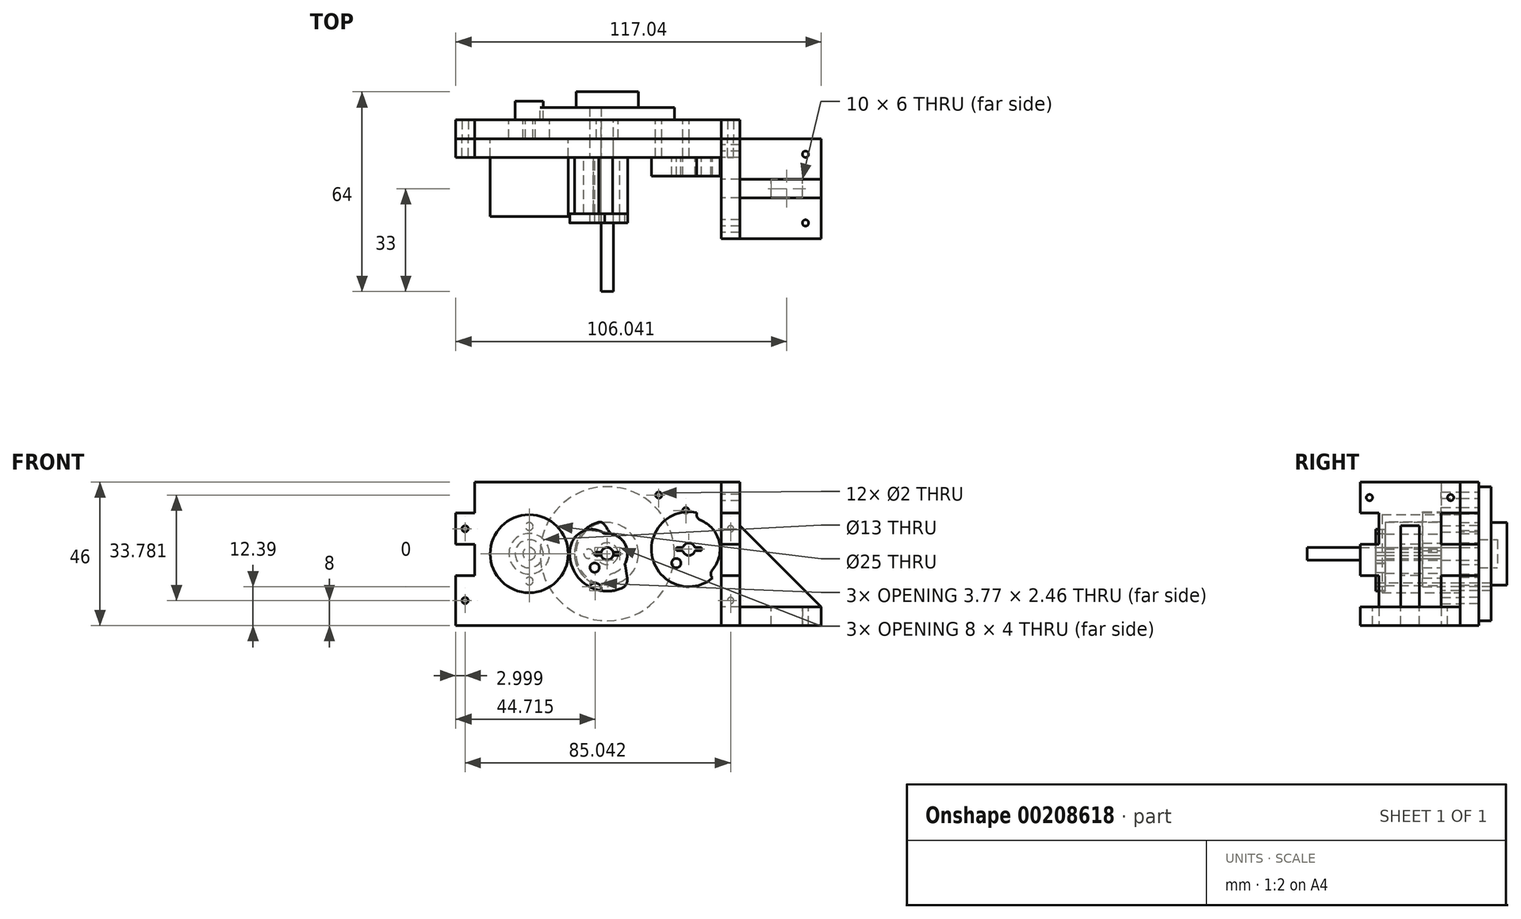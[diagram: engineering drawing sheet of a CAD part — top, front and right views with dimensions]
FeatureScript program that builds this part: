
annotation { "Feature Type Name" : "Feature", "Feature Type Description" : "" }
export const myFeature = defineFeature(function(context is Context, id is Id, definition is map)
    precondition{}
    {
        {
            var Q0;
            Q0=qCreatedBy(makeId("Front.planeOp"),FACE);
            var sketch = newSketch(context, id + "F0", { "sketchPlane" : qUnion([Q0])});
            skLineSegment(sketch, "E0.bottom", {"start": v(36.52, 23) * mm, "end": v(-42.52, 23) * mm});
            skLineSegment(sketch, "E0.top", {"start": v(42.52, -23) * mm, "end": v(-48.52, -23) * mm});
            skPoint(sketch, "E0.middle", {"position": v(0, 0) * mm});
            skCircle(sketch, "E1", {"center": v(-25, 0) * mm, "radius": 6.5 * mm});
            skLineSegment(sketch, "E2", {"start": v(-25, 8.75) * mm, "end": v(-25, -8.75) * mm, "construction": true});
            skCircle(sketch, "E3", {"center": v(-25, 8.75) * mm, "radius": 1.25 * mm});
            skCircle(sketch, "E4", {"center": v(-25, -8.75) * mm, "radius": 1.25 * mm});
            skCircle(sketch, "E5", {"center": v(0, 0) * mm, "radius": 3.5 * mm});
            skCircle(sketch, "E6", {"center": v(-25, 0) * mm, "radius": 12.5 * mm, "construction": true});
            skCircle(sketch, "E7", {"center": v(16.5, 18.78) * mm, "radius": 1 * mm});
            skCircle(sketch, "E8", {"center": v(25.19, 13.81) * mm, "radius": 1 * mm});
            skLineSegment(sketch, "E9", {"start": v(25.19, 13.81) * mm, "end": v(16.5, 18.78) * mm, "construction": true});
            skLineSegment(sketch, "E10.bottom", {"start": v(8.2, 14.32) * mm, "end": v(13.16, 23) * mm, "construction": true});
            skLineSegment(sketch, "E10.top", {"start": v(25.55, 4.39) * mm, "end": v(30.52, 13.07) * mm, "construction": true});
            skLineSegment(sketch, "E10.left", {"start": v(8.2, 14.32) * mm, "end": v(25.55, 4.39) * mm, "construction": true});
            skLineSegment(sketch, "E10.right", {"start": v(13.16, 23) * mm, "end": v(30.52, 13.07) * mm, "construction": true});
            skLineSegment(sketch, "E11", {"start": v(21.84, 18.03) * mm, "end": v(20.85, 16.3) * mm, "construction": true});
            skCircle(sketch, "E12", {"center": v(0, 0) * mm, "radius": 6.5 * mm, "construction": true});
            skCircle(sketch, "E13", {"center": v(0, 0) * mm, "radius": 10.5 * mm, "construction": true});
            skLineSegment(sketch, "E14", {"start": v(36.52, 23) * mm, "end": v(36.52, 13) * mm});
            skLineSegment(sketch, "E15", {"start": v(36.52, 13) * mm, "end": v(42.52, 13) * mm});
            skLineSegment(sketch, "E16", {"start": v(42.52, 13) * mm, "end": v(42.52, 3) * mm});
            skLineSegment(sketch, "E17", {"start": v(42.52, 3) * mm, "end": v(36.52, 3) * mm});
            skLineSegment(sketch, "E18", {"start": v(36.52, 3) * mm, "end": v(36.52, -7) * mm});
            skLineSegment(sketch, "E19", {"start": v(36.52, -7) * mm, "end": v(42.52, -7) * mm});
            skLineSegment(sketch, "E20", {"start": v(42.52, -7) * mm, "end": v(42.52, -23) * mm});
            skCircle(sketch, "E21", {"center": v(0, 0) * mm, "radius": 21.5 * mm, "construction": true});
            skLineSegment(sketch, "E22", {"start": v(-3, -23) * mm, "end": v(-3, -27.3) * mm, "construction": true});
            skLineSegment(sketch, "E23.MirrorCS", {"start": v(-42.52, 23) * mm, "end": v(-42.52, 13) * mm});
            skLineSegment(sketch, "E24.MirrorCS", {"start": v(-42.52, 13) * mm, "end": v(-48.52, 13) * mm});
            skLineSegment(sketch, "E25.MirrorCS", {"start": v(-48.52, 13) * mm, "end": v(-48.52, 3) * mm});
            skLineSegment(sketch, "E26.MirrorCS", {"start": v(-48.52, 3) * mm, "end": v(-42.52, 3) * mm});
            skLineSegment(sketch, "E27.MirrorCS", {"start": v(-42.52, 3) * mm, "end": v(-42.52, -7) * mm});
            skLineSegment(sketch, "E28.MirrorCS", {"start": v(-42.52, -7) * mm, "end": v(-48.52, -7) * mm});
            skLineSegment(sketch, "E29.MirrorCS", {"start": v(-48.52, -7) * mm, "end": v(-48.52, -23) * mm});
            skSolve(sketch);
        }
        {
            var Q0;
            Q0 = qSketchRegion(id + "F0", true);
            extrude(context, id + "F1", {"entities" : qUnion([Q0]), "depth" : 6 * mm});
        }
        {
            var Q0;
            Q0=qCreatedBy(makeId("Top.planeOp"),FACE);
            var sketch = newSketch(context, id + "F2", { "sketchPlane" : qUnion([Q0])});
            skLineSegment(sketch, "E30", {"start": v(0, 9) * mm, "end": v(0, -55) * mm});
            skLineSegment(sketch, "E31", {"start": v(0, -55) * mm, "end": v(2, -55) * mm});
            skLineSegment(sketch, "E32", {"start": v(2, -55) * mm, "end": v(2, 0) * mm});
            skLineSegment(sketch, "E33", {"start": v(2, 0) * mm, "end": v(21.5, 0) * mm});
            skLineSegment(sketch, "E34", {"start": v(21.5, 0) * mm, "end": v(21.5, 4) * mm});
            skLineSegment(sketch, "E35", {"start": v(21.5, 4) * mm, "end": v(10, 4) * mm});
            skLineSegment(sketch, "E36", {"start": v(10, 4) * mm, "end": v(10, 9) * mm});
            skLineSegment(sketch, "E37", {"start": v(10, 9) * mm, "end": v(0, 9) * mm});
            skSolve(sketch);
        }
        {
            var Q0;
            Q0 = qSketchRegion(id + "F2", true);
            var Q1;
            Q1=sQuery(id+"F2.wireOp",EDGE,"E30");
            revolve(context, id + "F3", {"entities" : qUnion([Q0]), "axis" : qUnion([Q1]), "revolveType" : RevolveType.FULL});
        }
        {
            var Q0;
            Q0=qCreatedBy(makeId("Top.planeOp"),FACE);
            var sketch = newSketch(context, id + "F4", { "sketchPlane" : qUnion([Q0])});
            skLineSegment(sketch, "E38", {"start": v(-12.5, -31) * mm, "end": v(-12.5, -6) * mm});
            skLineSegment(sketch, "E39", {"start": v(-12.5, -6) * mm, "end": v(-23, -6) * mm});
            skLineSegment(sketch, "E40", {"start": v(-23, -6) * mm, "end": v(-23, 0) * mm});
            skLineSegment(sketch, "E41", {"start": v(-23, 0) * mm, "end": v(-20.5, 0) * mm});
            skLineSegment(sketch, "E42", {"start": v(-20.5, 0) * mm, "end": v(-20.5, 6) * mm});
            skLineSegment(sketch, "E43", {"start": v(-20.5, 6) * mm, "end": v(-25, 6) * mm});
            skLineSegment(sketch, "E44", {"start": v(-25, 6) * mm, "end": v(-25, -31) * mm});
            skLineSegment(sketch, "E45", {"start": v(-25, -31) * mm, "end": v(-12.5, -31) * mm});
            skSolve(sketch);
        }
        {
            var Q0;
            Q0 = qSketchRegion(id + "F4", true);
            var Q1;
            Q1=sQuery(id+"F4.wireOp",EDGE,"E44");
            revolve(context, id + "F5", {"entities" : qUnion([Q0]), "axis" : qUnion([Q1]), "revolveType" : RevolveType.FULL});
        }
        {
            var Q0;
            Q0=makeQuery(id+"F1.opExtrude","CAP_FACE",FACE,{"disambiguationData":[OSD([sQuery(id+"F0.wireOp",EDGE,"E0.bottom"),sQuery(id+"F0.wireOp",EDGE,"E0.top"),sQuery(id+"F0.wireOp",EDGE,"E0.left"),sQuery(id+"F0.wireOp",EDGE,"E0.right"),sQuery(id+"F0.wireOp",EDGE,"E1"),sQuery(id+"F0.wireOp",EDGE,"E3"),sQuery(id+"F0.wireOp",EDGE,"E4"),sQuery(id+"F0.wireOp",EDGE,"E5")])],"isStart":false});
            var sketch = newSketch(context, id + "F6", { "sketchPlane" : qUnion([Q0])});
            skCircle(sketch, "E46", {"center": v(0, 0) * mm, "radius": 2 * mm});
            skCircle(sketch, "E47", {"center": v(-25, 0) * mm, "radius": 12.5 * mm});
            skCircle(sketch, "E48", {"center": v(16.5, 18.78) * mm, "radius": 1 * mm});
            skCircle(sketch, "E49", {"center": v(25.19, 13.81) * mm, "radius": 1 * mm});
            skLineSegment(sketch, "E50", {"start": v(36.52, 23) * mm, "end": v(36.52, 13) * mm});
            skLineSegment(sketch, "E51", {"start": v(36.52, 13) * mm, "end": v(42.52, 13) * mm});
            skLineSegment(sketch, "E52", {"start": v(42.52, 13) * mm, "end": v(42.52, 3) * mm});
            skLineSegment(sketch, "E53", {"start": v(42.52, 3) * mm, "end": v(36.52, 3) * mm});
            skLineSegment(sketch, "E54", {"start": v(36.52, 3) * mm, "end": v(36.52, -7) * mm});
            skLineSegment(sketch, "E55", {"start": v(36.52, -7) * mm, "end": v(42.52, -7) * mm});
            skLineSegment(sketch, "E56", {"start": v(42.52, -7) * mm, "end": v(42.52, -23) * mm});
            skLineSegment(sketch, "E57", {"start": v(42.52, -23) * mm, "end": v(-48.52, -23) * mm});
            skLineSegment(sketch, "E58", {"start": v(-48.52, -23) * mm, "end": v(-48.52, -7) * mm});
            skLineSegment(sketch, "E59", {"start": v(-48.52, -7) * mm, "end": v(-42.52, -7) * mm});
            skLineSegment(sketch, "E60", {"start": v(-42.52, -7) * mm, "end": v(-42.52, 3) * mm});
            skLineSegment(sketch, "E61", {"start": v(-42.52, 3) * mm, "end": v(-48.52, 3) * mm});
            skLineSegment(sketch, "E62", {"start": v(-48.52, 3) * mm, "end": v(-48.52, 13) * mm});
            skLineSegment(sketch, "E63", {"start": v(-48.52, 13) * mm, "end": v(-42.52, 13) * mm});
            skLineSegment(sketch, "E64", {"start": v(-42.52, 13) * mm, "end": v(-42.52, 23) * mm});
            skLineSegment(sketch, "E65", {"start": v(-42.52, 23) * mm, "end": v(36.52, 23) * mm});
            skLineSegment(sketch, "E66", {"start": v(42.52, 13) * mm, "end": v(36.52, 3) * mm, "construction": true});
            skLineSegment(sketch, "E67", {"start": v(42.52, -23) * mm, "end": v(36.52, -7) * mm, "construction": true});
            skCircle(sketch, "E68", {"center": v(39.52, -15) * mm, "radius": 1 * mm});
            skCircle(sketch, "E69", {"center": v(39.52, 8) * mm, "radius": 1 * mm});
            skLineSegment(sketch, "E70", {"start": v(-48.52, -23) * mm, "end": v(-42.52, -7) * mm, "construction": true});
            skLineSegment(sketch, "E71", {"start": v(-42.52, 3) * mm, "end": v(-48.52, 13) * mm, "construction": true});
            skCircle(sketch, "E72", {"center": v(-45.52, 8) * mm, "radius": 1 * mm});
            skCircle(sketch, "E73", {"center": v(-45.52, -15) * mm, "radius": 1 * mm});
            skSolve(sketch);
        }
        {
            var Q0;
            Q0 = qSketchRegion(id + "F6", true);
            extrude(context, id + "F7", {"entities" : qUnion([Q0]), "depth" : 6 * mm});
        }
        {
            var Q0;
            Q0=sQuery(id+"F6.wireOp",VERTEX,"E69.center");
            var Q1;
            Q1=sQuery(id+"F6.wireOp",VERTEX,"E68.center");
            var Q2;
            Q2=sQuery(id+"F6.wireOp",VERTEX,"E73.center");
            var Q3;
            Q3=sQuery(id+"F6.wireOp",VERTEX,"E72.center");
            var Q4;
            Q4=makeQuery(id+"F1.opExtrude","SWEPT_BODY",BODY,{"disambiguationData":[OSD([sQuery(id+"F0.wireOp",EDGE,"E0.bottom"),sQuery(id+"F0.wireOp",EDGE,"E0.top"),sQuery(id+"F0.wireOp",EDGE,"E1"),sQuery(id+"F0.wireOp",EDGE,"E3"),sQuery(id+"F0.wireOp",EDGE,"E4"),sQuery(id+"F0.wireOp",EDGE,"E5"),sQuery(id+"F0.wireOp",EDGE,"E7"),sQuery(id+"F0.wireOp",EDGE,"E8"),sQuery(id+"F0.wireOp",EDGE,"E14"),sQuery(id+"F0.wireOp",EDGE,"E15"),sQuery(id+"F0.wireOp",EDGE,"E16"),sQuery(id+"F0.wireOp",EDGE,"E17"),sQuery(id+"F0.wireOp",EDGE,"E18"),sQuery(id+"F0.wireOp",EDGE,"E19"),sQuery(id+"F0.wireOp",EDGE,"E20"),sQuery(id+"F0.wireOp",EDGE,"E23.MirrorCS"),sQuery(id+"F0.wireOp",EDGE,"E24.MirrorCS"),sQuery(id+"F0.wireOp",EDGE,"E25.MirrorCS"),sQuery(id+"F0.wireOp",EDGE,"E26.MirrorCS"),sQuery(id+"F0.wireOp",EDGE,"E27.MirrorCS"),sQuery(id+"F0.wireOp",EDGE,"E28.MirrorCS"),sQuery(id+"F0.wireOp",EDGE,"E29.MirrorCS")])]});
            hole(context, id + "F8", {"style" : HoleStyle.SIMPLE, "endStyle" : HoleEndStyle.THROUGH, "holeDiameter" : 2 * mm, "locations" : qUnion([Q0, Q1, Q2, Q3]), "scope" : qUnion([Q4]), "isTappedThrough" : true});
        }
        {
            var Q0;
            Q0=makeQuery(id+"F7.opExtrude","CAP_FACE",FACE,{"disambiguationData":[OSD([sQuery(id+"F6.wireOp",EDGE,"E46"),sQuery(id+"F6.wireOp",EDGE,"E47"),sQuery(id+"F6.wireOp",EDGE,"lmgn0v4Y-SyGt-rFrS-4Csl-fsZQkOtd9OQq.bottom"),sQuery(id+"F6.wireOp",EDGE,"lmgn0v4Y-SyGt-rFrS-4Csl-fsZQkOtd9OQq.top"),sQuery(id+"F6.wireOp",EDGE,"lmgn0v4Y-SyGt-rFrS-4Csl-fsZQkOtd9OQq.left"),sQuery(id+"F6.wireOp",EDGE,"lmgn0v4Y-SyGt-rFrS-4Csl-fsZQkOtd9OQq.right"),sQuery(id+"F6.wireOp",EDGE,"E48"),sQuery(id+"F6.wireOp",EDGE,"E49")])],"isStart":false});
            var sketch = newSketch(context, id + "F9", { "sketchPlane" : qUnion([Q0])});
            skArc(sketch, "E74", {"start": v(-1.94, -0.5) * mm, "mid": v(0, -2) * mm, "end": v(1.94, -0.5) * mm});
            skLineSegment(sketch, "E75", {"start": v(0, 0) * mm, "end": v(14.02, 0) * mm, "construction": true});
            skLineSegment(sketch, "E76", {"start": v(0, 0) * mm, "end": v(-2.72, 10.14) * mm, "construction": true});
            skLineSegment(sketch, "E77", {"start": v(0, 0) * mm, "end": v(-2.72, -10.14) * mm, "construction": true});
            skLineSegment(sketch, "E78", {"start": v(1.68, 6.28) * mm, "end": v(0, 0) * mm, "construction": true});
            skLineSegment(sketch, "E79", {"start": v(0, 0) * mm, "end": v(1.68, -6.28) * mm, "construction": true});
            skArc(sketch, "E80", {"start": v(1.68, -6.28) * mm, "mid": v(6.5, 0) * mm, "end": v(1.68, 6.28) * mm});
            skArc(sketch, "E81", {"start": v(-2.72, -10.14) * mm, "mid": v(-10.5, 0) * mm, "end": v(-2.72, 10.14) * mm});
            skFitSpline(sketch, "E82", {"points": [v(-2.72, 10.14) * mm, v(1.68, 6.28) * mm], "startDerivative": vector(7.02, 1.05) * mm, "endDerivative": vector(4.97, -0.66) * mm});
            skFitSpline(sketch, "E83.MirrorCS", {"points": [v(-2.72, -10.14) * mm, v(1.68, -6.28) * mm], "startDerivative": vector(7.02, -1.05) * mm, "endDerivative": vector(4.97, 0.66) * mm});
            skLineSegment(sketch, "E84.bottom", {"start": v(4, -0.5) * mm, "end": v(1.94, -0.5) * mm});
            skLineSegment(sketch, "E84.top", {"start": v(4, 0.5) * mm, "end": v(1.94, 0.5) * mm});
            skLineSegment(sketch, "E84.left", {"start": v(4, -0.5) * mm, "end": v(4, 0.5) * mm});
            skLineSegment(sketch, "E84.right", {"start": v(-4, -0.5) * mm, "end": v(-4, 0.5) * mm});
            skLineSegment(sketch, "E85.trimOffspring", {"start": v(-1.94, 0.5) * mm, "end": v(-4, 0.5) * mm});
            skLineSegment(sketch, "E86.trimOffspring", {"start": v(0.13, 0.5) * mm, "end": v(-0.13, 0.5) * mm});
            skLineSegment(sketch, "E87.trimOffspring", {"start": v(0.13, -0.5) * mm, "end": v(-0.13, -0.5) * mm});
            skLineSegment(sketch, "E88.trimOffspring", {"start": v(-1.94, -0.5) * mm, "end": v(-4, -0.5) * mm});
            skArc(sketch, "E89.trimOffspring", {"start": v(1.94, 0.5) * mm, "mid": v(0, 2) * mm, "end": v(-1.94, 0.5) * mm});
            skLineSegment(sketch, "E90", {"start": v(0, 0) * mm, "end": v(-6, 0) * mm, "construction": true});
            skCircle(sketch, "E91", {"center": v(-6, 0) * mm, "radius": 1.5 * mm});
            skSolve(sketch);
        }
        {
            var Q0;
            Q0 = qSketchRegion(id + "F9", true);
            extrude(context, id + "F10", {"entities" : qUnion([Q0]), "depth" : 18 * mm});
        }
        {
            var Q0;
            Q0=makeQuery(id+"F7.opExtrude","SWEPT_FACE",FACE,{"disambiguationData":[OSD([sQuery(id+"F6.wireOp",EDGE,"E50")])]});
            var sketch = newSketch(context, id + "F11", { "sketchPlane" : qUnion([Q0])});
            skLineSegment(sketch, "E92", {"start": v(-6, 23) * mm, "end": v(-6, 13) * mm});
            skLineSegment(sketch, "E93", {"start": v(-6, 13) * mm, "end": v(-12, 13) * mm});
            skLineSegment(sketch, "E94", {"start": v(-12, 13) * mm, "end": v(-12, 3) * mm});
            skLineSegment(sketch, "E95", {"start": v(-12, 3) * mm, "end": v(-6, 3) * mm});
            skLineSegment(sketch, "E96", {"start": v(-6, 3) * mm, "end": v(-6, -7) * mm});
            skLineSegment(sketch, "E97", {"start": v(-6, -7) * mm, "end": v(-12, -7) * mm});
            skLineSegment(sketch, "E98", {"start": v(-12, -7) * mm, "end": v(-12, -23) * mm});
            skLineSegment(sketch, "E99", {"start": v(-12, -23) * mm, "end": v(-19, -23) * mm});
            skLineSegment(sketch, "E100", {"start": v(-22, -23) * mm, "end": v(-22, 23) * mm, "construction": true});
            skLineSegment(sketch, "E101", {"start": v(-6, 23) * mm, "end": v(-22, 23) * mm});
            skLineSegment(sketch, "E102.MirrorCS", {"start": v(-32, 3) * mm, "end": v(-38, 3) * mm});
            skLineSegment(sketch, "E103.MirrorCS", {"start": v(-38, 3) * mm, "end": v(-38, -7) * mm});
            skLineSegment(sketch, "E104.MirrorCS", {"start": v(-32, 13) * mm, "end": v(-32, 3) * mm});
            skLineSegment(sketch, "E105.MirrorCS", {"start": v(-38, -7) * mm, "end": v(-32, -7) * mm});
            skLineSegment(sketch, "E106.MirrorCS", {"start": v(-32, -7) * mm, "end": v(-32, -23) * mm});
            skLineSegment(sketch, "E107.MirrorCS", {"start": v(-38, 13) * mm, "end": v(-32, 13) * mm});
            skLineSegment(sketch, "E108.MirrorCS", {"start": v(-38, 23) * mm, "end": v(-38, 13) * mm});
            skLineSegment(sketch, "E109.MirrorCS", {"start": v(-32, -23) * mm, "end": v(-25, -23) * mm});
            skLineSegment(sketch, "E110.MirrorCS", {"start": v(-38, 23) * mm, "end": v(-22, 23) * mm});
            skLineSegment(sketch, "E111", {"start": v(-19, -23) * mm, "end": v(-19, -17) * mm});
            skLineSegment(sketch, "E112", {"start": v(-19, -17) * mm, "end": v(-22, -17) * mm});
            skLineSegment(sketch, "E113.MirrorCS", {"start": v(-25, -17) * mm, "end": v(-22, -17) * mm});
            skLineSegment(sketch, "E114.MirrorCS", {"start": v(-25, -23) * mm, "end": v(-25, -17) * mm});
            skPoint(sketch, "E115.orphan", {"position": v(-22, -23) * mm});
            skLineSegment(sketch, "E116.bottom", {"start": v(-19, -7) * mm, "end": v(-25, -7) * mm});
            skLineSegment(sketch, "E116.top", {"start": v(-19, 3) * mm, "end": v(-25, 3) * mm});
            skLineSegment(sketch, "E116.left", {"start": v(-19, -7) * mm, "end": v(-19, 3) * mm});
            skLineSegment(sketch, "E116.right", {"start": v(-25, -7) * mm, "end": v(-25, 3) * mm});
            skPoint(sketch, "E116.middle", {"position": v(-22, -2) * mm});
            skCircle(sketch, "E117", {"center": v(-9, 18) * mm, "radius": 1 * mm});
            skPoint(sketch, "E117.centerSnap0", {"position": v(-12, 18) * mm});
            skLineSegment(sketch, "E118", {"start": v(-9, 18) * mm, "end": v(-35, 18) * mm, "construction": true});
            skCircle(sketch, "E119", {"center": v(-35, 18) * mm, "radius": 1 * mm});
            skPoint(sketch, "E120", {"position": v(-22, 18) * mm});
            skSolve(sketch);
        }
        {
            var Q0;
            Q0 = qSketchRegion(id + "F11", true);
            extrude(context, id + "F12", {"entities" : qUnion([Q0]), "depth" : 6 * mm});
        }
        {
            var Q0;
            Q0=makeQuery(id+"F12.opExtrude","SWEPT_FACE",FACE,{"disambiguationData":[OSD([sQuery(id+"F11.wireOp",EDGE,"E112"),sQuery(id+"F11.wireOp",EDGE,"E113.MirrorCS")])]});
            var sketch = newSketch(context, id + "F13", { "sketchPlane" : qUnion([Q0])});
            skLineSegment(sketch, "E121", {"start": v(42.52, 25) * mm, "end": v(36.52, 25) * mm});
            skLineSegment(sketch, "E122", {"start": v(36.52, 25) * mm, "end": v(36.52, 19) * mm});
            skLineSegment(sketch, "E123", {"start": v(36.52, 19) * mm, "end": v(42.52, 19) * mm});
            skLineSegment(sketch, "E124", {"start": v(42.52, 19) * mm, "end": v(42.52, 6) * mm});
            skLineSegment(sketch, "E125", {"start": v(42.52, 6) * mm, "end": v(68.52, 6) * mm});
            skLineSegment(sketch, "E126", {"start": v(68.52, 6) * mm, "end": v(68.52, 38) * mm});
            skLineSegment(sketch, "E127", {"start": v(68.52, 38) * mm, "end": v(42.52, 38) * mm});
            skLineSegment(sketch, "E128", {"start": v(42.52, 38) * mm, "end": v(42.52, 25) * mm});
            skLineSegment(sketch, "E129", {"start": v(42.52, 22) * mm, "end": v(57.52, 22) * mm, "construction": true});
            skLineSegment(sketch, "E130.bottom", {"start": v(62.52, 25) * mm, "end": v(52.52, 25) * mm});
            skLineSegment(sketch, "E130.top", {"start": v(62.52, 19) * mm, "end": v(52.52, 19) * mm});
            skLineSegment(sketch, "E130.left", {"start": v(62.52, 25) * mm, "end": v(62.52, 19) * mm});
            skLineSegment(sketch, "E130.right", {"start": v(52.52, 25) * mm, "end": v(52.52, 19) * mm});
            skPoint(sketch, "E130.middle", {"position": v(57.52, 22) * mm});
            skCircle(sketch, "E131", {"center": v(63.52, 33) * mm, "radius": 1 * mm});
            skCircle(sketch, "E132", {"center": v(63.52, 11) * mm, "radius": 1 * mm});
            skSolve(sketch);
        }
        {
            var Q0;
            Q0 = qSketchRegion(id + "F13", true);
            extrude(context, id + "F14", {"entities" : qUnion([Q0]), "depth" : 6 * mm});
        }
        {
            var Q0;
            Q0=makeQuery(id+"F12.opExtrude","SWEPT_FACE",FACE,{"disambiguationData":[OSD([sQuery(id+"F11.wireOp",EDGE,"E116.left")])]});
            var sketch = newSketch(context, id + "F15", { "sketchPlane" : qUnion([Q0])});
            skLineSegment(sketch, "E133", {"start": v(68.52, -17) * mm, "end": v(62.52, -17) * mm});
            skLineSegment(sketch, "E134", {"start": v(62.52, -17) * mm, "end": v(62.52, -23) * mm});
            skLineSegment(sketch, "E135", {"start": v(62.52, -23) * mm, "end": v(52.52, -23) * mm});
            skLineSegment(sketch, "E136", {"start": v(52.52, -23) * mm, "end": v(52.52, -17) * mm});
            skLineSegment(sketch, "E137", {"start": v(52.52, -17) * mm, "end": v(42.52, -17) * mm});
            skLineSegment(sketch, "E138", {"start": v(42.52, -17) * mm, "end": v(42.52, -7) * mm});
            skLineSegment(sketch, "E139", {"start": v(42.52, -7) * mm, "end": v(36.52, -7) * mm});
            skLineSegment(sketch, "E140", {"start": v(36.52, -7) * mm, "end": v(36.52, 3) * mm});
            skLineSegment(sketch, "E141", {"start": v(36.52, 3) * mm, "end": v(42.52, 3) * mm});
            skLineSegment(sketch, "E142", {"start": v(42.52, 3) * mm, "end": v(42.52, 9) * mm});
            skLineSegment(sketch, "E143", {"start": v(42.52, 9) * mm, "end": v(68.52, -17) * mm});
            skSolve(sketch);
        }
        {
            var Q0;
            Q0 = qSketchRegion(id + "F15", true);
            extrude(context, id + "F16", {"entities" : qUnion([Q0]), "depth" : 6 * mm});
        }
        {
            var Q0;
            Q0=makeQuery(id+"F10.opExtrude","CAP_FACE",FACE,{"disambiguationData":[OSD([sQuery(id+"F9.wireOp",EDGE,"E74"),sQuery(id+"F9.wireOp",EDGE,"E80"),sQuery(id+"F9.wireOp",EDGE,"E81"),sQuery(id+"F9.wireOp",EDGE,"E82"),sQuery(id+"F9.wireOp",EDGE,"E83.MirrorCS"),sQuery(id+"F9.wireOp",EDGE,"E84.bottom"),sQuery(id+"F9.wireOp",EDGE,"E84.top"),sQuery(id+"F9.wireOp",EDGE,"E84.left"),sQuery(id+"F9.wireOp",EDGE,"E84.right"),sQuery(id+"F9.wireOp",EDGE,"E85.trimOffspring"),sQuery(id+"F9.wireOp",EDGE,"E88.trimOffspring"),sQuery(id+"F9.wireOp",EDGE,"E89.trimOffspring"),sQuery(id+"F9.wireOp",EDGE,"E91")])],"isStart":false});
            var sketch = newSketch(context, id + "F17", { "sketchPlane" : qUnion([Q0])});
            skLineSegment(sketch, "E144", {"start": v(-4, 0.5) * mm, "end": v(-1.94, 0.5) * mm});
            skLineSegment(sketch, "E145", {"start": v(-4, 0.5) * mm, "end": v(-4, -0.5) * mm});
            skLineSegment(sketch, "E146", {"start": v(-4, -0.5) * mm, "end": v(-1.94, -0.5) * mm});
            skLineSegment(sketch, "E147", {"start": v(1.94, -0.5) * mm, "end": v(4, -0.5) * mm});
            skLineSegment(sketch, "E148", {"start": v(4, -0.5) * mm, "end": v(4, 0.5) * mm});
            skLineSegment(sketch, "E149", {"start": v(4, 0.5) * mm, "end": v(1.94, 0.5) * mm});
            skArc(sketch, "E150", {"start": v(-1.94, 0.5) * mm, "mid": v(0, 2) * mm, "end": v(1.94, 0.5) * mm});
            skArc(sketch, "E151", {"start": v(1.94, -0.5) * mm, "mid": v(0, -2) * mm, "end": v(-1.94, -0.5) * mm});
            skCircle(sketch, "E152", {"center": v(-4.02, -4.45) * mm, "radius": 1.5 * mm});
            skArc(sketch, "E153", {"start": v(-6.72, 9.94) * mm, "mid": v(-9.94, -6.72) * mm, "end": v(6.72, -9.94) * mm});
            skArc(sketch, "E154", {"start": v(5.72, -3.1) * mm, "mid": v(5.38, 3.64) * mm, "end": v(-0.75, 6.46) * mm});
            skLineSegment(sketch, "E155", {"start": v(6.72, -9.94) * mm, "end": v(-6.72, 9.94) * mm, "construction": true});
            skLineSegment(sketch, "E156", {"start": v(-1.28, 7.25) * mm, "end": v(7.66, -5.98) * mm, "construction": true});
            skLineSegment(sketch, "E157", {"start": v(-6.72, 9.94) * mm, "end": v(-0.75, 6.46) * mm});
            skLineSegment(sketch, "E158", {"start": v(6.72, -9.94) * mm, "end": v(5.72, -3.1) * mm});
            skSolve(sketch);
        }
        {
            var Q0;
            Q0 = qSketchRegion(id + "F17", true);
            extrude(context, id + "F18", {"entities" : qUnion([Q0]), "depth" : 3 * mm});
        }
        {
            var Q0;
            Q0=makeQuery(id+"F18.opExtrude","SWEPT_EDGE",EDGE,{"disambiguationData":[OSD([sQuery(id+"F17.wireOp",EDGE,"E153"),sQuery(id+"F17.wireOp",EDGE,"E158")])]});
            var Q1;
            Q1=makeQuery(id+"FKJxsdPJaydyWRq_9.opExtrude","SWEPT_EDGE",EDGE,{"disambiguationData":[OSD([sQuery(id+"F17.wireOp",EDGE,"E153"),sQuery(id+"F17.wireOp",EDGE,"E158")])]});
            fillet(context, id + "F19", {"entities" : qUnion([Q0, Q1]), "radius" : 3 * mm, "tangentPropagation" : true, "allowEdgeOverflow" : false});
        }
        {
            var Q0;
            Q0=makeQuery(id+"F18.opExtrude","SWEPT_EDGE",EDGE,{"disambiguationData":[OSD([sQuery(id+"F17.wireOp",EDGE,"E153"),sQuery(id+"F17.wireOp",EDGE,"E157")])]});
            fillet(context, id + "F20", {"entities" : qUnion([Q0]), "radius" : 7 * mm, "tangentPropagation" : true, "allowEdgeOverflow" : false});
        }
        {
            var Q0;
            Q0=makeQuery(id+"F18.opExtrude","CAP_FACE",FACE,{"disambiguationData":[OSD([sQuery(id+"F17.wireOp",EDGE,"E144"),sQuery(id+"F17.wireOp",EDGE,"E145"),sQuery(id+"F17.wireOp",EDGE,"E146"),sQuery(id+"F17.wireOp",EDGE,"E147"),sQuery(id+"F17.wireOp",EDGE,"E148"),sQuery(id+"F17.wireOp",EDGE,"E149"),sQuery(id+"F17.wireOp",EDGE,"E150"),sQuery(id+"F17.wireOp",EDGE,"E151"),sQuery(id+"F17.wireOp",EDGE,"E152"),sQuery(id+"F17.wireOp",EDGE,"E153"),sQuery(id+"F17.wireOp",EDGE,"E154"),sQuery(id+"F17.wireOp",EDGE,"E157"),sQuery(id+"F17.wireOp",EDGE,"E158")])],"isStart":false});
            var sketch = newSketch(context, id + "F21", { "sketchPlane" : qUnion([Q0])});
            skArc(sketch, "E159", {"start": v(-1.96, -11.84) * mm, "mid": v(-3.24, -9.49) * mm, "end": v(-5.7, -10.56) * mm});
            skArc(sketch, "E160", {"start": v(-5.7, -10.56) * mm, "mid": v(-3.88, -11.36) * mm, "end": v(-1.96, -11.84) * mm});
            skSolve(sketch);
        }
        {
            var Q0;
            Q0 = qSketchRegion(id + "F21", true);
            extrude(context, id + "F22", {"entities" : qUnion([Q0]), "operationType" : NewBodyOperationType.REMOVE, "endBound" : BoundingType.THROUGH_ALL, "oppositeDirection" : true, "depth" : 25 * mm});
        }
        {
            var Q0;
            Q0=makeQuery(id+"F7.opExtrude","CAP_FACE",FACE,{"disambiguationData":[OSD([sQuery(id+"F6.wireOp",EDGE,"E46"),sQuery(id+"F6.wireOp",EDGE,"E47"),sQuery(id+"F6.wireOp",EDGE,"E48"),sQuery(id+"F6.wireOp",EDGE,"E49"),sQuery(id+"F6.wireOp",EDGE,"E50"),sQuery(id+"F6.wireOp",EDGE,"E51"),sQuery(id+"F6.wireOp",EDGE,"E52"),sQuery(id+"F6.wireOp",EDGE,"E53"),sQuery(id+"F6.wireOp",EDGE,"E54"),sQuery(id+"F6.wireOp",EDGE,"E55"),sQuery(id+"F6.wireOp",EDGE,"E56"),sQuery(id+"F6.wireOp",EDGE,"E57"),sQuery(id+"F6.wireOp",EDGE,"E58"),sQuery(id+"F6.wireOp",EDGE,"E59"),sQuery(id+"F6.wireOp",EDGE,"E60"),sQuery(id+"F6.wireOp",EDGE,"E61"),sQuery(id+"F6.wireOp",EDGE,"E62"),sQuery(id+"F6.wireOp",EDGE,"E63"),sQuery(id+"F6.wireOp",EDGE,"E64"),sQuery(id+"F6.wireOp",EDGE,"E65"),sQuery(id+"F6.wireOp",EDGE,"E68"),sQuery(id+"F6.wireOp",EDGE,"E69"),sQuery(id+"F6.wireOp",EDGE,"E72"),sQuery(id+"F6.wireOp",EDGE,"E73")])],"isStart":false});
            var sketch = newSketch(context, id + "F23", { "sketchPlane" : qUnion([Q0])});
            skLineSegment(sketch, "E161", {"start": v(22.16, 1.96) * mm, "end": v(24.22, 1.96) * mm});
            skLineSegment(sketch, "E162", {"start": v(22.16, 1.96) * mm, "end": v(22.16, 0.96) * mm});
            skLineSegment(sketch, "E163", {"start": v(22.16, 0.96) * mm, "end": v(24.22, 0.96) * mm});
            skLineSegment(sketch, "E164", {"start": v(28.1, 0.96) * mm, "end": v(30.16, 0.96) * mm});
            skLineSegment(sketch, "E165", {"start": v(30.16, 0.96) * mm, "end": v(30.16, 1.96) * mm});
            skLineSegment(sketch, "E166", {"start": v(30.16, 1.96) * mm, "end": v(28.1, 1.96) * mm});
            skArc(sketch, "E167", {"start": v(24.22, 1.96) * mm, "mid": v(26.16, 3.46) * mm, "end": v(28.1, 1.96) * mm});
            skArc(sketch, "E168", {"start": v(28.1, 0.96) * mm, "mid": v(26.16, -0.54) * mm, "end": v(24.22, 0.96) * mm});
            skCircle(sketch, "E169", {"center": v(22.13, -2.99) * mm, "radius": 1.5 * mm});
            skArc(sketch, "E170", {"start": v(28.71, 13.19) * mm, "mid": v(14.49, -1.33) * mm, "end": v(33.74, -7.83) * mm});
            skArc(sketch, "E171", {"start": v(28.71, 13.19) * mm, "mid": v(28.82, 11.74) * mm, "end": v(29.88, 10.75) * mm});
            skArc(sketch, "E172", {"start": v(33.68, -5.13) * mm, "mid": v(33.18, -6.5) * mm, "end": v(33.74, -7.83) * mm});
            skArc(sketch, "E173", {"start": v(33.68, -5.13) * mm, "mid": v(35.88, 3.8) * mm, "end": v(29.88, 10.75) * mm});
            skSolve(sketch);
        }
        {
            var Q0;
            Q0 = qSketchRegion(id + "F23", true);
            extrude(context, id + "F24", {"entities" : qUnion([Q0]), "depth" : 6 * mm});
        }
    });
